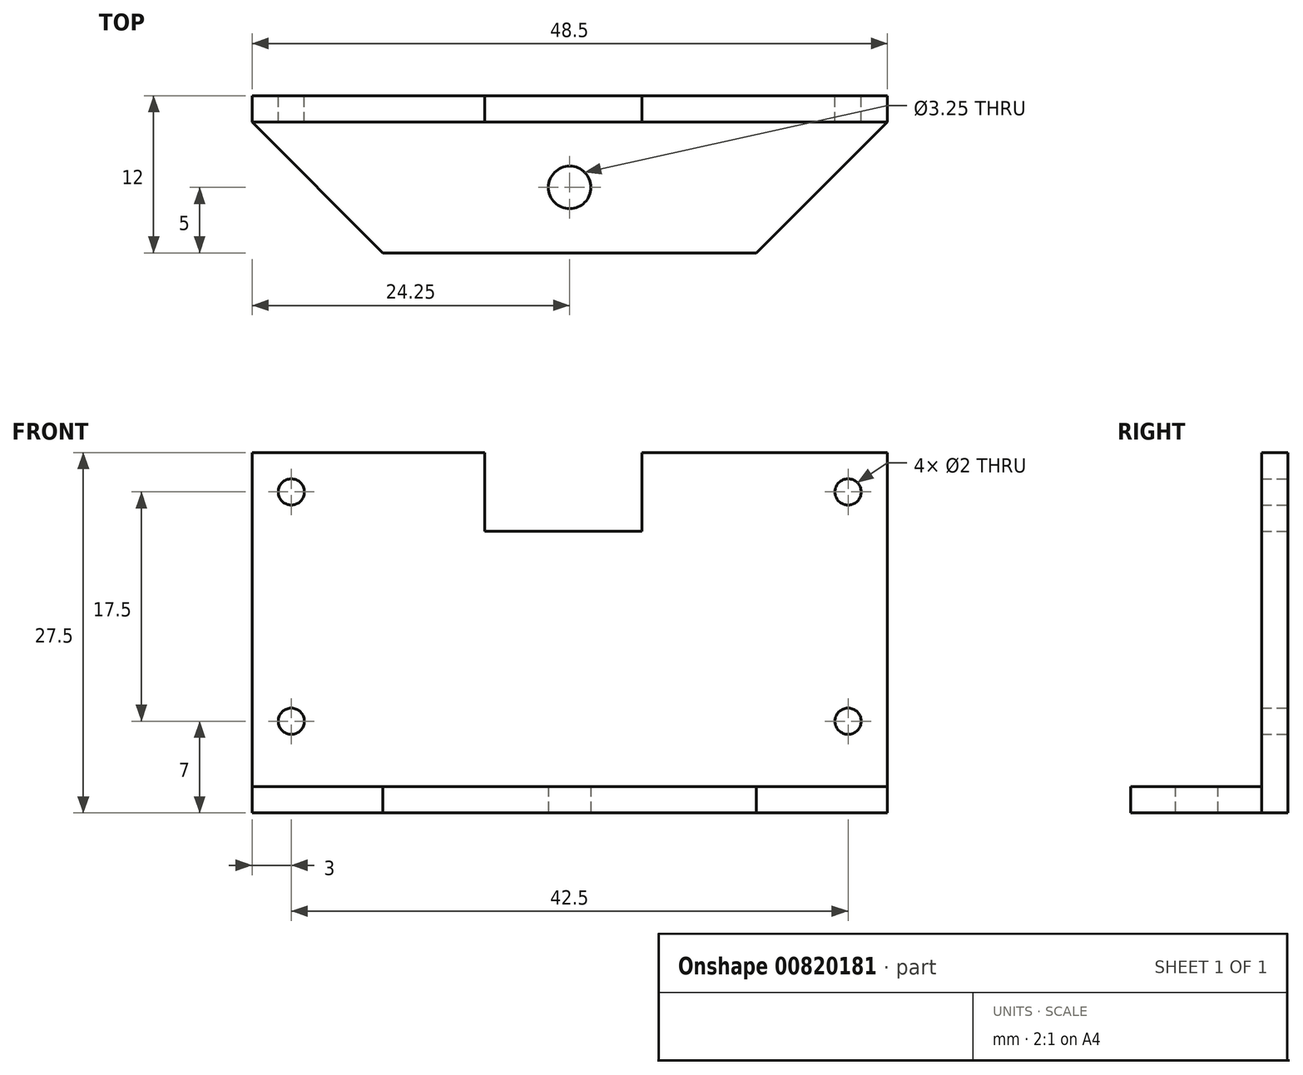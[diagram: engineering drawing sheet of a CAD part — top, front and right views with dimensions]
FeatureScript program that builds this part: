
annotation { "Feature Type Name" : "Feature", "Feature Type Description" : "" }
export const myFeature = defineFeature(function(context is Context, id is Id, definition is map)
    precondition{}
    {
        {
            var Q0;
            Q0=qCreatedBy(makeId("Front.planeOp"),FACE);
            var sketch = newSketch(context, id + "F0", { "sketchPlane" : qUnion([Q0])});
            skLineSegment(sketch, "E0.bottom", {"start": v(-24.25, -13.75) * mm, "end": v(24.25, -13.75) * mm});
            skLineSegment(sketch, "E0.top", {"start": v(-24.25, 11.75) * mm, "end": v(-6.48, 11.75) * mm});
            skLineSegment(sketch, "E0.left", {"start": v(-24.25, -13.75) * mm, "end": v(-24.25, 11.75) * mm});
            skLineSegment(sketch, "E0.right", {"start": v(24.25, -13.75) * mm, "end": v(24.25, 11.75) * mm});
            skPoint(sketch, "E0.middle", {"position": v(0, -1) * mm});
            skLineSegment(sketch, "E1", {"start": v(5.52, 11.75) * mm, "end": v(24.25, 11.75) * mm});
            skLineSegment(sketch, "E2", {"start": v(-6.48, 11.75) * mm, "end": v(-6.48, 5.75) * mm});
            skLineSegment(sketch, "E3", {"start": v(-6.48, 5.75) * mm, "end": v(5.52, 5.75) * mm});
            skLineSegment(sketch, "E4", {"start": v(5.52, 5.75) * mm, "end": v(5.52, 11.75) * mm});
            skPoint(sketch, "E5", {"position": v(-21.25, 8.75) * mm});
            skPoint(sketch, "E6", {"position": v(-21.25, -8.75) * mm});
            skPoint(sketch, "E7", {"position": v(21.25, -8.75) * mm});
            skPoint(sketch, "E8", {"position": v(21.25, 8.75) * mm});
            skSolve(sketch);
        }
        {
            var Q0;
            Q0=qCreatedBy(makeId("Front.planeOp"),FACE);
            var sketch = newSketch(context, id + "F1", { "sketchPlane" : qUnion([Q0])});
            skLineSegment(sketch, "E9.bottom", {"start": v(24.25, -13.75) * mm, "end": v(-24.25, -13.75) * mm});
            skLineSegment(sketch, "E9.top", {"start": v(24.25, -15.75) * mm, "end": v(-24.25, -15.75) * mm});
            skLineSegment(sketch, "E9.left", {"start": v(24.25, -13.75) * mm, "end": v(24.25, -15.75) * mm});
            skLineSegment(sketch, "E9.right", {"start": v(-24.25, -13.75) * mm, "end": v(-24.25, -15.75) * mm});
            skSolve(sketch);
        }
        {
            var Q0;
            Q0=makeQuery(id+"F0.imprint","IMPRINT",FACE,{"disambiguationData":[TD([[makeQuery(id+"F0.imprint","IMPRINT",EDGE,{"derivedFrom":sQuery(id+"F0.wireOp",EDGE,"E0.bottom")}),1.0]])]});
            extrude(context, id + "F2", {"entities" : qUnion([Q0]), "depth" : 2 * mm, "offsetDistance" : 25 * mm});
        }
        {
            var Q0;
            Q0=sQuery(id+"F0.wireOp",VERTEX,"E5");
            var Q1;
            Q1=makeQuery(id+"F2.opExtrude","SWEPT_BODY",BODY,{"disambiguationData":[OSD([sQuery(id+"F0.wireOp",EDGE,"E0.bottom"),sQuery(id+"F0.wireOp",EDGE,"E0.top"),sQuery(id+"F0.wireOp",EDGE,"E0.left"),sQuery(id+"F0.wireOp",EDGE,"E0.right"),sQuery(id+"F0.wireOp",EDGE,"E1"),sQuery(id+"F0.wireOp",EDGE,"E2"),sQuery(id+"F0.wireOp",EDGE,"E3"),sQuery(id+"F0.wireOp",EDGE,"E4")])]});
            hole(context, id + "F3", {"style" : HoleStyle.SIMPLE, "endStyle" : HoleEndStyle.THROUGH, "oppositeDirection" : true, "holeDiameter" : 2 * mm, "majorDiameter" : 5 * mm, "isTappedThrough" : true, "tappedDepth" : 12 * mm, "tapClearance" : 3, "locations" : qUnion([Q0]), "scope" : qUnion([Q1])});
        }
        {
            var Q0;
            Q0=sQuery(id+"F0.wireOp",VERTEX,"E6");
            var Q1;
            Q1=makeQuery(id+"F2.opExtrude","SWEPT_BODY",BODY,{"disambiguationData":[OSD([sQuery(id+"F0.wireOp",EDGE,"E0.bottom"),sQuery(id+"F0.wireOp",EDGE,"E0.top"),sQuery(id+"F0.wireOp",EDGE,"E0.left"),sQuery(id+"F0.wireOp",EDGE,"E0.right"),sQuery(id+"F0.wireOp",EDGE,"E1"),sQuery(id+"F0.wireOp",EDGE,"E2"),sQuery(id+"F0.wireOp",EDGE,"E3"),sQuery(id+"F0.wireOp",EDGE,"E4")])]});
            hole(context, id + "F4", {"style" : HoleStyle.SIMPLE, "endStyle" : HoleEndStyle.THROUGH, "oppositeDirection" : true, "holeDiameter" : 2 * mm, "majorDiameter" : 5 * mm, "isTappedThrough" : true, "tappedDepth" : 12 * mm, "tapClearance" : 3, "locations" : qUnion([Q0]), "scope" : qUnion([Q1])});
        }
        {
            var Q0;
            Q0=sQuery(id+"F0.wireOp",VERTEX,"E8");
            var Q1;
            Q1=makeQuery(id+"F2.opExtrude","SWEPT_BODY",BODY,{"disambiguationData":[OSD([sQuery(id+"F0.wireOp",EDGE,"E0.bottom"),sQuery(id+"F0.wireOp",EDGE,"E0.top"),sQuery(id+"F0.wireOp",EDGE,"E0.left"),sQuery(id+"F0.wireOp",EDGE,"E0.right"),sQuery(id+"F0.wireOp",EDGE,"E1"),sQuery(id+"F0.wireOp",EDGE,"E2"),sQuery(id+"F0.wireOp",EDGE,"E3"),sQuery(id+"F0.wireOp",EDGE,"E4")])]});
            hole(context, id + "F5", {"style" : HoleStyle.SIMPLE, "endStyle" : HoleEndStyle.THROUGH, "oppositeDirection" : true, "holeDiameter" : 2 * mm, "majorDiameter" : 5 * mm, "isTappedThrough" : true, "tappedDepth" : 12 * mm, "tapClearance" : 3, "locations" : qUnion([Q0]), "scope" : qUnion([Q1])});
        }
        {
            var Q0;
            Q0=sQuery(id+"F0.wireOp",VERTEX,"E7");
            var Q1;
            Q1=makeQuery(id+"F2.opExtrude","SWEPT_BODY",BODY,{"disambiguationData":[OSD([sQuery(id+"F0.wireOp",EDGE,"E0.bottom"),sQuery(id+"F0.wireOp",EDGE,"E0.top"),sQuery(id+"F0.wireOp",EDGE,"E0.left"),sQuery(id+"F0.wireOp",EDGE,"E0.right"),sQuery(id+"F0.wireOp",EDGE,"E1"),sQuery(id+"F0.wireOp",EDGE,"E2"),sQuery(id+"F0.wireOp",EDGE,"E3"),sQuery(id+"F0.wireOp",EDGE,"E4")])]});
            hole(context, id + "F6", {"style" : HoleStyle.SIMPLE, "endStyle" : HoleEndStyle.THROUGH, "oppositeDirection" : true, "holeDiameter" : 2 * mm, "majorDiameter" : 5 * mm, "isTappedThrough" : true, "tappedDepth" : 12 * mm, "tapClearance" : 3, "locations" : qUnion([Q0]), "scope" : qUnion([Q1])});
        }
        {
            var Q0;
            Q0=makeQuery(id+"F1.imprint","IMPRINT",FACE,{"disambiguationData":[TD([[makeQuery(id+"F1.imprint","IMPRINT",EDGE,{"derivedFrom":sQuery(id+"F1.wireOp",EDGE,"E9.bottom")}),1.0]])]});
            extrude(context, id + "F7", {"entities" : qUnion([Q0]), "operationType" : NewBodyOperationType.ADD, "depth" : 12 * mm, "offsetDistance" : 25 * mm});
        }
        {
            var Q0;
            Q0=makeQuery(id+"F7.opExtrude","CAP_EDGE",EDGE,{"disambiguationData":[OSD([sQuery(id+"F1.wireOp",EDGE,"E9.left")])],"isStart":false});
            chamfer(context, id + "F8", {"entities" : qUnion([Q0]), "width" : 10 * mm, "tangentPropagation" : true});
        }
        {
            var Q0;
            Q0=makeQuery(id+"F7.opExtrude","CAP_EDGE",EDGE,{"disambiguationData":[OSD([sQuery(id+"F1.wireOp",EDGE,"E9.right")])],"isStart":false});
            chamfer(context, id + "F9", {"entities" : qUnion([Q0]), "width" : 10 * mm, "tangentPropagation" : true});
        }
        {
            var Q0;
            Q0=makeQuery(id+"F7.opExtrude","SWEPT_FACE",FACE,{"disambiguationData":[OSD([sQuery(id+"F1.wireOp",EDGE,"E9.top")])]});
            cPlane(context, id + "F10", {"entities" : qUnion([Q0]), "cplaneType" : CPlaneType.OFFSET, "offset" : 0 * mm, "width" : 150 * mm, "height" : 150 * mm});
        }
        {
            var Q0;
            Q0=qCreatedBy(id+"F10.planeOp",FACE);
            var sketch = newSketch(context, id + "F11", { "sketchPlane" : qUnion([Q0])});
            skPoint(sketch, "E10", {"position": v(0, 7) * mm});
            skSolve(sketch);
        }
        {
            var Q0;
            Q0=sQuery(id+"F11.wireOp",VERTEX,"E10");
            var Q1;
            Q1=makeQuery(id+"F2.opExtrude","SWEPT_BODY",BODY,{"disambiguationData":[OSD([sQuery(id+"F0.wireOp",EDGE,"E0.bottom"),sQuery(id+"F0.wireOp",EDGE,"E0.top"),sQuery(id+"F0.wireOp",EDGE,"E0.left"),sQuery(id+"F0.wireOp",EDGE,"E0.right"),sQuery(id+"F0.wireOp",EDGE,"E1"),sQuery(id+"F0.wireOp",EDGE,"E2"),sQuery(id+"F0.wireOp",EDGE,"E3"),sQuery(id+"F0.wireOp",EDGE,"E4")])]});
            hole(context, id + "F12", {"style" : HoleStyle.SIMPLE, "endStyle" : HoleEndStyle.THROUGH, "holeDiameter" : 3.25 * mm, "majorDiameter" : 5 * mm, "isTappedThrough" : true, "tappedDepth" : 12 * mm, "tapClearance" : 3, "locations" : qUnion([Q0]), "scope" : qUnion([Q1])});
        }
    });
